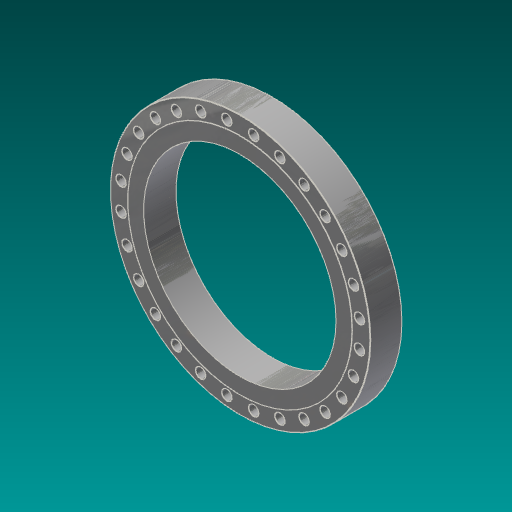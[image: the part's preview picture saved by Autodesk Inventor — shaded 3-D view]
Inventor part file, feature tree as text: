
AUTODESK INVENTOR PART (.ipt)
format: ipt  version: 2017.3 (Build 213257000, 257)  size: 275,456 bytes
history: native  units: in
note: dims shown in document units (in); Inventor stores cm internally (conversion verified against a paired STEP export)
features: sketch x3, extrude x2, chamfer x2, hole x1, pattern_circular x1
ambient origin geometry x8: Origin, YZ Plane, XZ Plane, XY Plane, X Axis, Y Axis, Z Axis, Center Point
bodies: Solid1 (feature_tree)
feature tree (9):
  extrude  "Extrusion1"  Depth=30.875in
  hole  "Hole1"  [1 undecoded]
  chamfer  "Chamfer1"  Distance=11.0236in Angle=360.0deg
  pattern_circular  "Circular Pattern1"  Angle=45.0deg  [1 undecoded]
  extrude  "Extrusion2"  Depth=0.0625in TaperAngle=45.0deg
  chamfer  "Chamfer2"  Distance=36.0in
  sketch  "Sketch1"  dims[d0=41.75in d1=30.875in]
  sketch  "Sketch2"  dims[d2=5.125in d3=0.0in d4=38.5in]
  sketch  "Sketch3"  dims[d5=0.0442in d6=1.625in d7=0.75in d8=0.375in d9=0.25in d10=0.5635in d11=1.0in d12=0.8108in d13=11.0236in d14=360.0deg d16=0.0312in d17=0.125in d18=45.0deg d19=0.0625in d20=0.125in d21=45.0deg d25=36.0in d26=0.0625in d27=0.0in]
note: 2 required parameter values undecoded (feature->parameter linkage not recoverable at this tier; creation-order binding heuristic only, values carry confidence <= 0.55)
